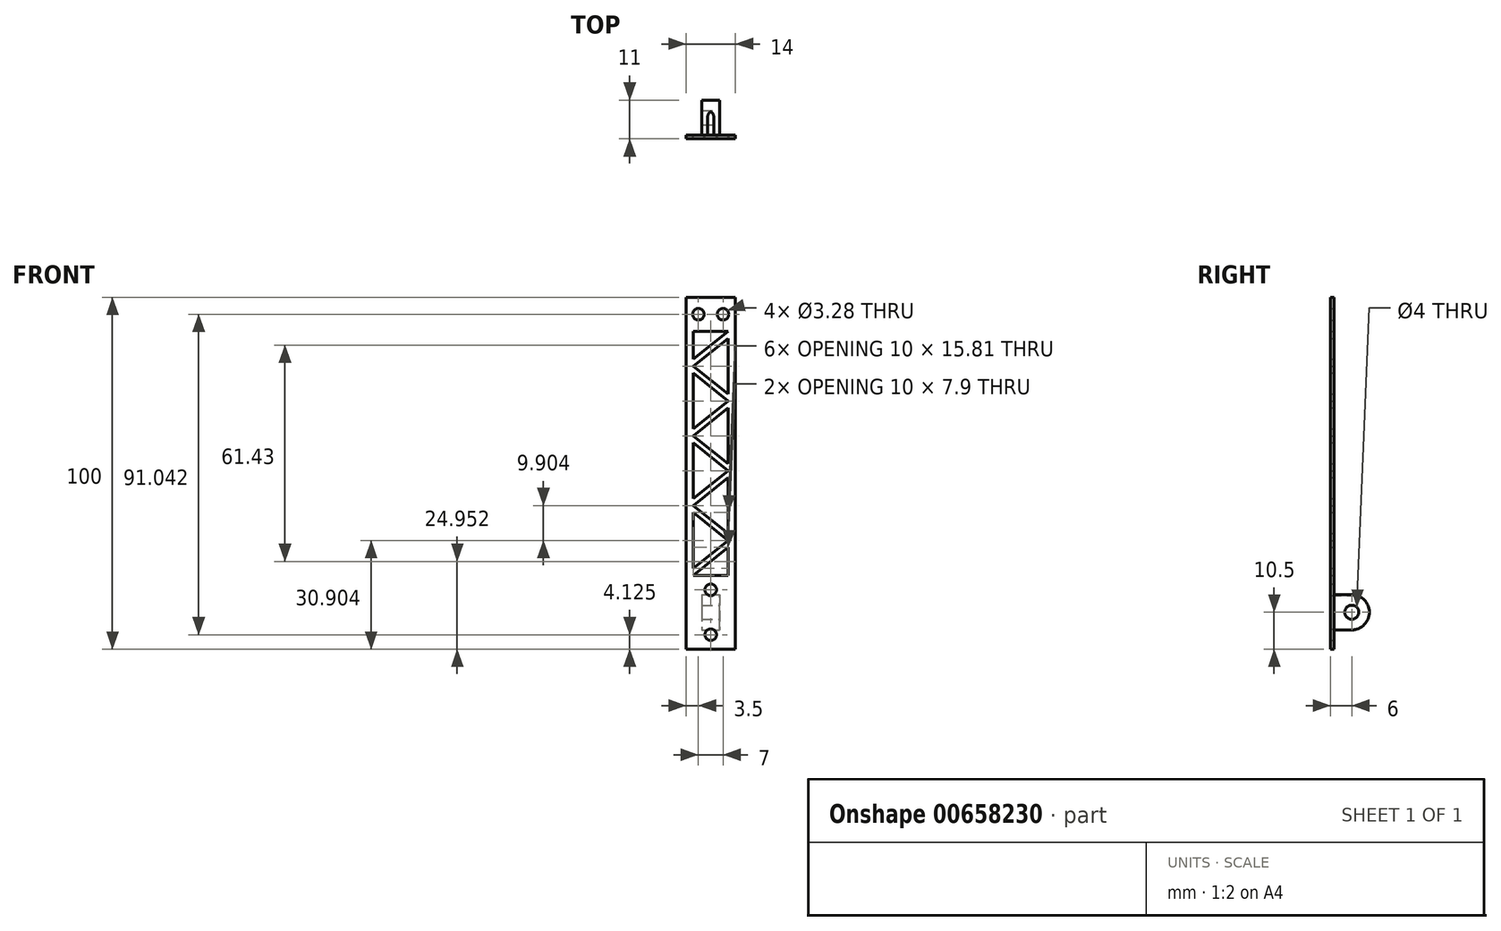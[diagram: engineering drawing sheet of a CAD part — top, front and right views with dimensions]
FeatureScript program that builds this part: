
annotation { "Feature Type Name" : "Feature", "Feature Type Description" : "" }
export const myFeature = defineFeature(function(context is Context, id is Id, definition is map)
    precondition{}
    {
        {
            var Q0;
            Q0=qCreatedBy(makeId("Front.planeOp"),FACE);
            var sketch = newSketch(context, id + "F0", { "sketchPlane" : qUnion([Q0])});
            skPoint(sketch, "E0.middle", {"position": v(0, 0) * mm});
            skLineSegment(sketch, "E1.top", {"start": v(-7, -50) * mm, "end": v(7, -50) * mm});
            skLineSegment(sketch, "E1.right", {"start": v(7, 50) * mm, "end": v(7, -50) * mm});
            skLineSegment(sketch, "E2.0", {"start": v(-2.5, -34.5) * mm, "end": v(-0.9, -34.5) * mm});
            skLineSegment(sketch, "E3.0", {"start": v(-2.5, -44.5) * mm, "end": v(-0.9, -44.5) * mm});
            skLineSegment(sketch, "E4", {"start": v(2.5, -34.5) * mm, "end": v(2.5, -44.5) * mm});
            skLineSegment(sketch, "E5", {"start": v(-2.5, -34.5) * mm, "end": v(-2.5, -44.5) * mm});
            skLineSegment(sketch, "E6", {"start": v(6, 20.37) * mm, "end": v(6, 20.37) * mm});
            skLineSegment(sketch, "E7", {"start": v(-7, 50) * mm, "end": v(7, 50) * mm});
            skLineSegment(sketch, "E8", {"start": v(-7, -50) * mm, "end": v(-7, 50) * mm});
            skLineSegment(sketch, "E9", {"start": v(5, -29) * mm, "end": v(-5, -29) * mm});
            skLineSegment(sketch, "E10", {"start": v(-5, -29) * mm, "end": v(5, -21.1) * mm});
            skLineSegment(sketch, "E11", {"start": v(5, -21.1) * mm, "end": v(5, -29) * mm});
            skLineSegment(sketch, "E12", {"start": v(-5, -27) * mm, "end": v(5, -19.1) * mm});
            skLineSegment(sketch, "E13", {"start": v(-5, -11.2) * mm, "end": v(5, -19.1) * mm});
            skLineSegment(sketch, "E14", {"start": v(-5, -27) * mm, "end": v(-5, -11.2) * mm});
            skLineSegment(sketch, "E15", {"start": v(-5, -9.2) * mm, "end": v(5, -17.1) * mm});
            skLineSegment(sketch, "E16", {"start": v(5, -17.1) * mm, "end": v(5, -1.29) * mm});
            skLineSegment(sketch, "E17", {"start": v(5, -1.29) * mm, "end": v(-5, -9.2) * mm});
            skLineSegment(sketch, "E18.0.1.0", {"start": v(5, 2.71) * mm, "end": v(5, 18.52) * mm});
            skLineSegment(sketch, "E18.0.1.1", {"start": v(-5, 10.62) * mm, "end": v(5, 2.71) * mm});
            skLineSegment(sketch, "E18.0.1.2", {"start": v(-5, 8.62) * mm, "end": v(5, 0.71) * mm});
            skLineSegment(sketch, "E18.0.1.3", {"start": v(-5, -7.2) * mm, "end": v(5, 0.71) * mm});
            skLineSegment(sketch, "E18.0.1.4", {"start": v(5, 18.52) * mm, "end": v(-5, 10.62) * mm});
            skLineSegment(sketch, "E18.0.1.5", {"start": v(-5, -7.2) * mm, "end": v(-5, 8.62) * mm});
            skLineSegment(sketch, "E18.0.2.0", {"start": v(5, 22.52) * mm, "end": v(5, 38.33) * mm});
            skLineSegment(sketch, "E18.0.2.1", {"start": v(-5, 30.43) * mm, "end": v(5, 22.52) * mm});
            skLineSegment(sketch, "E18.0.2.2", {"start": v(-5, 28.43) * mm, "end": v(5, 20.52) * mm});
            skLineSegment(sketch, "E18.0.2.3", {"start": v(-5, 12.62) * mm, "end": v(5, 20.52) * mm});
            skLineSegment(sketch, "E18.0.2.4", {"start": v(5, 38.33) * mm, "end": v(-5, 30.43) * mm});
            skLineSegment(sketch, "E18.0.2.5", {"start": v(-5, 12.62) * mm, "end": v(-5, 28.43) * mm});
            skLineSegment(sketch, "E18.0.3.3", {"start": v(-5, 32.43) * mm, "end": v(5, 40.33) * mm});
            skLineSegment(sketch, "E18.0.3.5", {"start": v(-5, 32.43) * mm, "end": v(-5, 40.33) * mm});
            skLineSegment(sketch, "E19", {"start": v(5, 40.33) * mm, "end": v(-5, 40.33) * mm});
            skCircle(sketch, "E20", {"center": v(3.5, 45.17) * mm, "radius": 1.64 * mm});
            skCircle(sketch, "E21.MirrorC", {"center": v(-3.5, 45.17) * mm, "radius": 1.64 * mm});
            skCircle(sketch, "E22", {"center": v(0, -33.12) * mm, "radius": 1.64 * mm});
            skLineSegment(sketch, "E23.trimOffspring", {"start": v(0.9, -34.5) * mm, "end": v(2.5, -34.5) * mm});
            skCircle(sketch, "E24.MirrorC", {"center": v(0, -45.88) * mm, "radius": 1.64 * mm});
            skLineSegment(sketch, "E25.trimOffspring", {"start": v(0.9, -44.5) * mm, "end": v(2.5, -44.5) * mm});
            skSolve(sketch);
        }
        {
            var Q0;
            {var subQ5=sQuery(id+"F0.wireOp",EDGE,"E3.0");Q0=makeQuery(id+"F0.imprint","IMPRINT",FACE,{"disambiguationData":[TD([[makeQuery(id+"F0.imprint","IMPRINT",EDGE,{"derivedFrom":subQ5}),1.0]])]});}
            var Q1;
            Q1=makeQuery(id+"F0.imprint","IMPRINT",FACE,{"disambiguationData":[TD([[makeQuery(id+"F0.imprint","IMPRINT",EDGE,{"derivedFrom":sQuery(id+"F0.wireOp",EDGE,"E1.top")}),1.0]])]});
            extrude(context, id + "F1", {"entities" : qUnion([Q0, Q1]), "depth" : 1 * mm, "offsetDistance" : 25 * mm});
        }
        {
            var Q0;
            Q0=makeQuery(id+"F0.imprint","IMPRINT",FACE,{"disambiguationData":[TD([[makeQuery(id+"F0.imprint","IMPRINT",EDGE,{"derivedFrom":sQuery(id+"F0.wireOp",EDGE,"893792fe-0780-4b24-a035-615e8d3175d2")}),-1.0]])]});
            var Q1;
            {var subQ5=sQuery(id+"F0.wireOp",EDGE,"E3.0");Q1=makeQuery(id+"F0.imprint","IMPRINT",FACE,{"disambiguationData":[TD([[makeQuery(id+"F0.imprint","IMPRINT",EDGE,{"derivedFrom":subQ5}),1.0]])]});}
            var Q2;
            {var subQ0=sQuery(id+"F0.wireOp",EDGE,"E2.0");var subQ1=sQuery(id+"F0.wireOp",EDGE,"893792fe-0780-4b24-a035-615e8d3175d2");var subQ2=makeQuery(id+"F0.imprint","INTERSECT",VERTEX,{"disambiguationData":[OD(1.0)],"derivedFrom":[subQ1,subQ0]});Q2=makeQuery(id+"F0.imprint","IMPRINT",FACE,{"disambiguationData":[TD([[makeQuery(id+"F0.imprint","IMPRINT",EDGE,{"disambiguationData":[TD([[subQ2,-1.0]])],"derivedFrom":subQ1}),-1.0]])]});}
            var Q3;
            {var subQ0=sQuery(id+"F0.wireOp",EDGE,"E2.0");var subQ1=sQuery(id+"F0.wireOp",EDGE,"893792fe-0780-4b24-a035-615e8d3175d2");var subQ2=makeQuery(id+"F0.imprint","INTERSECT",VERTEX,{"disambiguationData":[OD(0.0)],"derivedFrom":[subQ1,subQ0]});Q3=makeQuery(id+"F0.imprint","IMPRINT",FACE,{"disambiguationData":[TD([[makeQuery(id+"F0.imprint","IMPRINT",EDGE,{"disambiguationData":[TD([[subQ2,1.0]])],"derivedFrom":subQ1}),1.0]])]});}
            extrude(context, id + "F2", {"entities" : qUnion([Q0, Q1, Q2, Q3]), "operationType" : NewBodyOperationType.ADD, "oppositeDirection" : true, "depth" : 10 * mm, "offsetDistance" : 25 * mm});
        }
        {
            var Q0;
            Q0=makeQuery(id+"F2.opExtrude","SWEPT_FACE",FACE,{"disambiguationData":[OSD([sQuery(id+"F0.wireOp",EDGE,"E4")])]});
            var sketch = newSketch(context, id + "F3", { "sketchPlane" : qUnion([Q0])});
            skCircle(sketch, "E26", {"center": v(5, -39.5) * mm, "radius": 2 * mm});
            skLineSegment(sketch, "E27", {"start": v(10, -44.5) * mm, "end": v(10, -34.5) * mm});
            skLineSegment(sketch, "E28", {"start": v(10, -34.5) * mm, "end": v(5, -34.5) * mm});
            skLineSegment(sketch, "E29", {"start": v(10, -44.5) * mm, "end": v(5, -44.5) * mm});
            skArc(sketch, "E30", {"start": v(5, -44.5) * mm, "mid": v(10, -39.5) * mm, "end": v(5, -34.5) * mm});
            skSolve(sketch);
        }
        {
            var Q0;
            {var subQ0=sQuery(id+"F3.wireOp",EDGE,"E29");Q0=makeQuery(id+"F3.imprint","IMPRINT",FACE,{"disambiguationData":[TD([[makeQuery(id+"F3.imprint","IMPRINT",EDGE,{"derivedFrom":subQ0}),-1.0]])]});}
            var Q1;
            Q1=makeQuery(id+"F3.imprint","IMPRINT",FACE,{"disambiguationData":[TD([[makeQuery(id+"F3.imprint","IMPRINT",EDGE,{"derivedFrom":sQuery(id+"F3.wireOp",EDGE,"E26")}),1.0]])]});
            var Q2;
            {var subQ0=sQuery(id+"F3.wireOp",EDGE,"E28");Q2=makeQuery(id+"F3.imprint","IMPRINT",FACE,{"disambiguationData":[TD([[makeQuery(id+"F3.imprint","IMPRINT",EDGE,{"derivedFrom":subQ0}),1.0]])]});}
            extrude(context, id + "F4", {"entities" : qUnion([Q0, Q1, Q2]), "operationType" : NewBodyOperationType.REMOVE, "endBound" : BoundingType.THROUGH_ALL, "oppositeDirection" : true, "depth" : 25 * mm, "offsetDistance" : 25 * mm});
        }
    });
